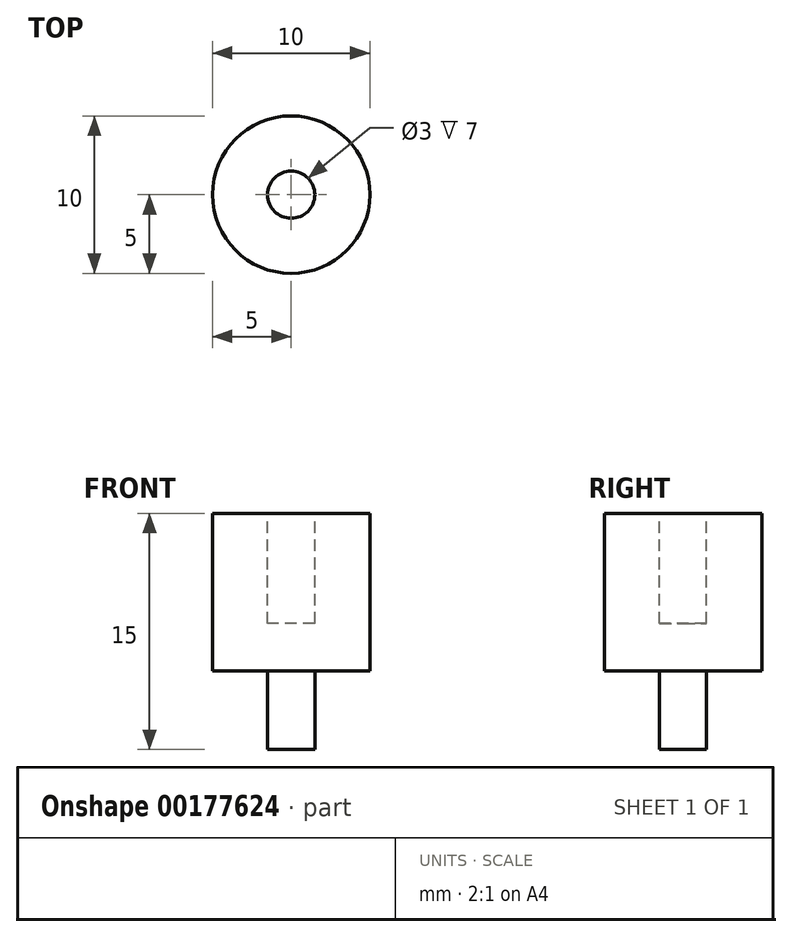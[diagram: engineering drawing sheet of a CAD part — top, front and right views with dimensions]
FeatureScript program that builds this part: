
annotation { "Feature Type Name" : "Feature", "Feature Type Description" : "" }
export const myFeature = defineFeature(function(context is Context, id is Id, definition is map)
    precondition{}
    {
        {
            var Q0;
            Q0=qCreatedBy(makeId("Top.planeOp"),FACE);
            var sketch = newSketch(context, id + "F0", { "sketchPlane" : qUnion([Q0])});
            skCircle(sketch, "E0", {"center": v(0, 0) * mm, "radius": 5 * mm});
            skSolve(sketch);
        }
        {
            var Q0;
            Q0 = qSketchRegion(id + "F0", true);
            extrude(context, id + "F1", {"entities" : qUnion([Q0]), "depth" : 10 * mm});
        }
        {
            var Q0;
            Q0=makeQuery(id+"F1.opExtrude","CAP_FACE",FACE,{"disambiguationData":[OSD([sQuery(id+"F0.wireOp",EDGE,"E0")])],"isStart":false});
            var sketch = newSketch(context, id + "F2", { "sketchPlane" : qUnion([Q0])});
            skCircle(sketch, "E1", {"center": v(0, 0) * mm, "radius": 1.5 * mm});
            skSolve(sketch);
        }
        {
            var Q0;
            Q0 = qSketchRegion(id + "F2", true);
            extrude(context, id + "F3", {"entities" : qUnion([Q0]), "operationType" : NewBodyOperationType.REMOVE, "oppositeDirection" : true, "depth" : 7 * mm});
        }
        {
            var Q0;
            Q0=makeQuery(id+"F1.opExtrude","CAP_FACE",FACE,{"disambiguationData":[OSD([sQuery(id+"F0.wireOp",EDGE,"E0")])],"isStart":true});
            var sketch = newSketch(context, id + "F4", { "sketchPlane" : qUnion([Q0])});
            skCircle(sketch, "E2", {"center": v(0, 0) * mm, "radius": 1.5 * mm});
            skSolve(sketch);
        }
        {
            var Q0;
            Q0 = qSketchRegion(id + "F4", true);
            extrude(context, id + "F5", {"entities" : qUnion([Q0]), "operationType" : NewBodyOperationType.ADD, "depth" : 5 * mm});
        }
    });
